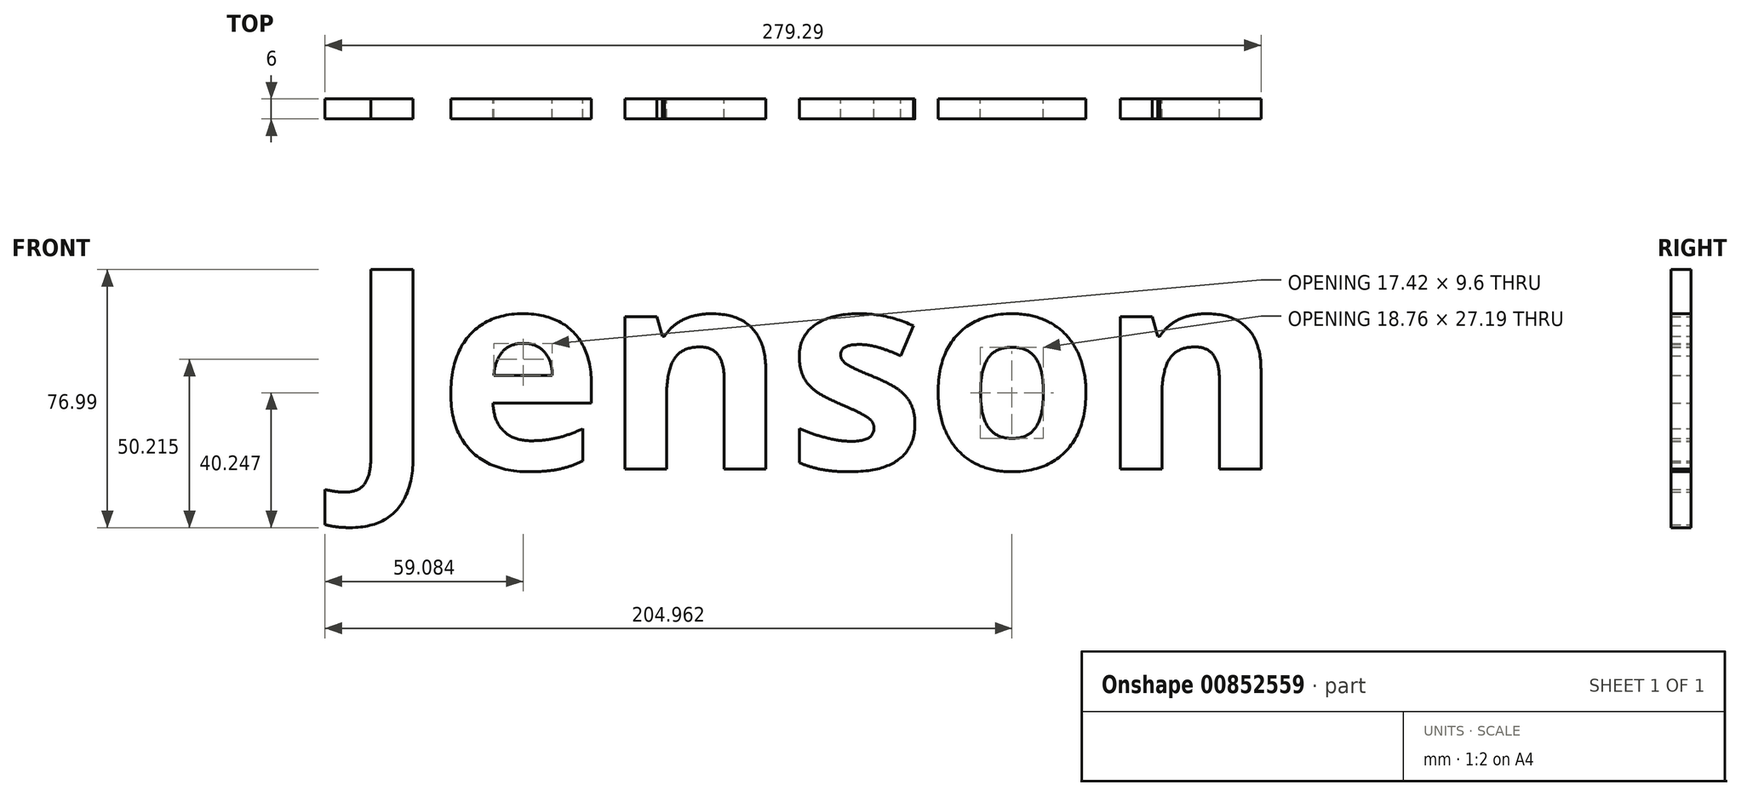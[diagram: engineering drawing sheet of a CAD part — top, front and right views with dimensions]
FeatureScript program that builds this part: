
annotation { "Feature Type Name" : "Feature", "Feature Type Description" : "" }
export const myFeature = defineFeature(function(context is Context, id is Id, definition is map)
    precondition{}
    {
        {
            var Q0;
            Q0=qCreatedBy(makeId("Front.planeOp"),FACE);
            var sketch = newSketch(context, id + "F0", { "sketchPlane" : qUnion([Q0])});
            skText(sketch, "E0", { "text": "Jenson", "fontName": "OpenSans-Bold.ttf"});
            const initialGuessF0  = {"E0": [-0.2847, -0.11484, 1, 0, 0.06]};
            skSetInitialGuess(sketch, initialGuessF0);
            skSolve(sketch);
        }
        {
            var Q0;
            Q0=makeQuery(id+"F0.imprint","IMPRINT",FACE,{"disambiguationData":[TD([[makeQuery(id+"F0.imprint","IMPRINT",EDGE,{"derivedFrom":sQuery(id+"F0.wireOp",EDGE,"E0.sketch_text.stroke-30")}),-1.0]])]});
            var Q1;
            Q1=makeQuery(id+"F0.imprint","IMPRINT",FACE,{"disambiguationData":[TD([[makeQuery(id+"F0.imprint","IMPRINT",EDGE,{"derivedFrom":sQuery(id+"F0.wireOp",EDGE,"E0.sketch_text.stroke-47")}),-1.0]])]});
            var Q2;
            Q2=makeQuery(id+"F0.imprint","IMPRINT",FACE,{"disambiguationData":[TD([[makeQuery(id+"F0.imprint","IMPRINT",EDGE,{"derivedFrom":sQuery(id+"F0.wireOp",EDGE,"E0.sketch_text.stroke-91")}),-1.0]])]});
            var Q3;
            Q3=makeQuery(id+"F0.imprint","IMPRINT",FACE,{"disambiguationData":[TD([[makeQuery(id+"F0.imprint","IMPRINT",EDGE,{"derivedFrom":sQuery(id+"F0.wireOp",EDGE,"E0.sketch_text.stroke-10")}),-1.0]])]});
            var Q4;
            Q4=makeQuery(id+"F0.imprint","IMPRINT",FACE,{"disambiguationData":[TD([[makeQuery(id+"F0.imprint","IMPRINT",EDGE,{"derivedFrom":sQuery(id+"F0.wireOp",EDGE,"E0.sketch_text.stroke-0")}),-1.0]])]});
            var Q5;
            Q5=makeQuery(id+"F0.imprint","IMPRINT",FACE,{"disambiguationData":[TD([[makeQuery(id+"F0.imprint","IMPRINT",EDGE,{"derivedFrom":sQuery(id+"F0.wireOp",EDGE,"E0.sketch_text.stroke-73")}),-1.0]])]});
            extrude(context, id + "F1", {"entities" : qUnion([Q0, Q1, Q2, Q3, Q4, Q5]), "depth" : 6 * mm, "offsetDistance" : 25 * mm});
        }
    });
